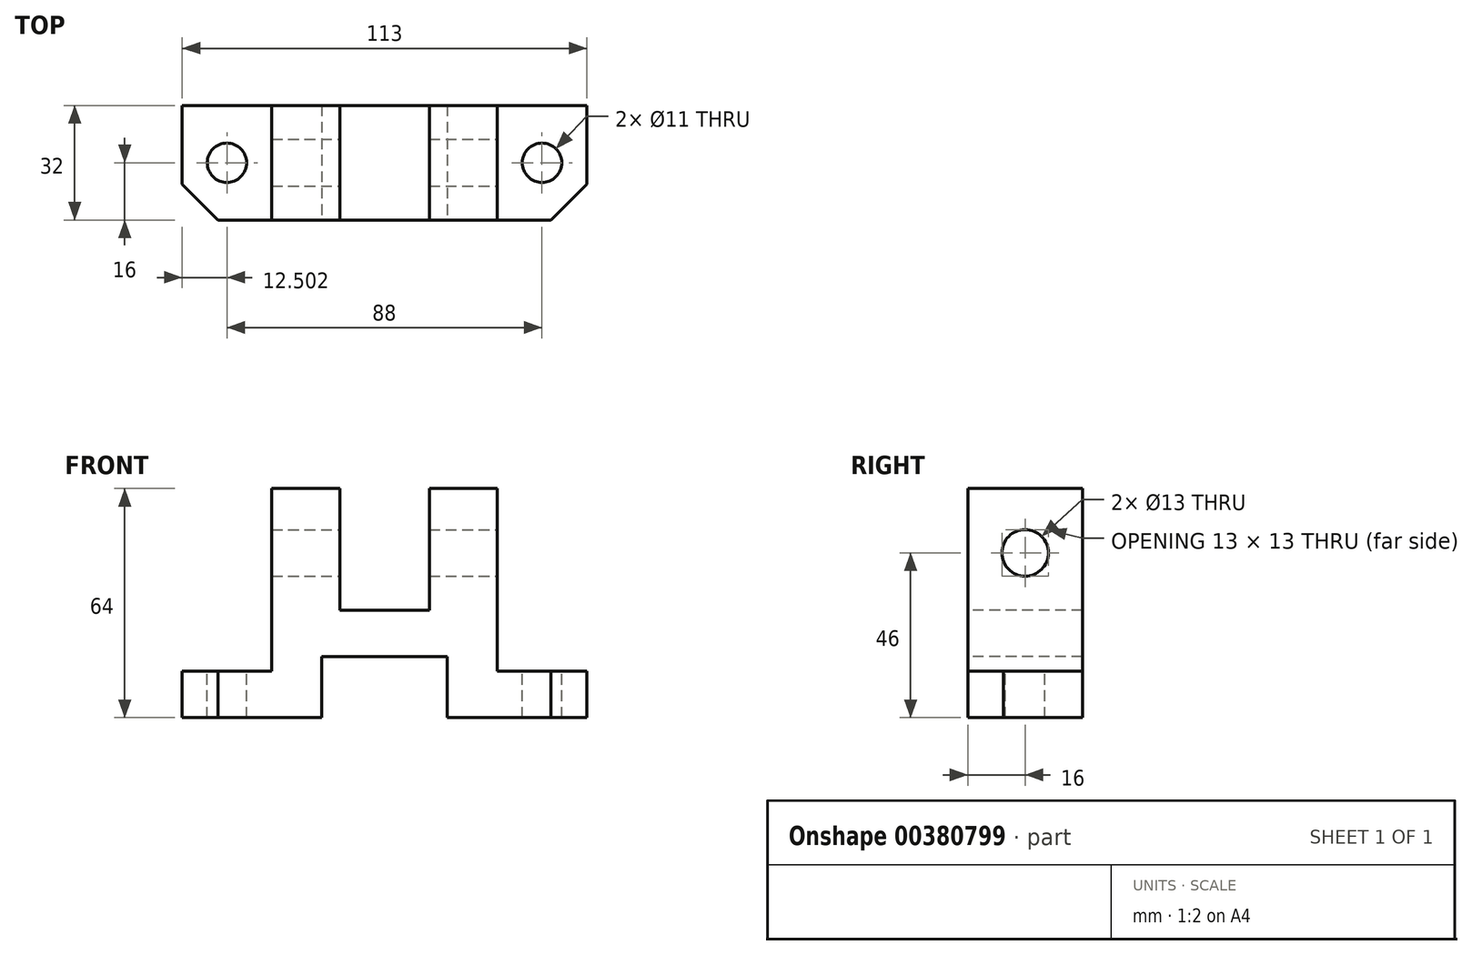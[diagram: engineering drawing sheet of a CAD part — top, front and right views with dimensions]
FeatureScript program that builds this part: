
annotation { "Feature Type Name" : "Feature", "Feature Type Description" : "" }
export const myFeature = defineFeature(function(context is Context, id is Id, definition is map)
    precondition{}
    {
        {
            var Q0;
            Q0=qCreatedBy(makeId("Top.planeOp"),FACE);
            var sketch = newSketch(context, id + "F0", { "sketchPlane" : qUnion([Q0])});
            skLineSegment(sketch, "E0", {"start": v(-42.78, 0) * mm, "end": v(70.22, 0) * mm});
            skLineSegment(sketch, "E1", {"start": v(70.22, 0) * mm, "end": v(70.22, 32) * mm});
            skLineSegment(sketch, "E2", {"start": v(70.22, 32) * mm, "end": v(-42.78, 32) * mm});
            skLineSegment(sketch, "E3", {"start": v(-42.78, 32) * mm, "end": v(-42.78, 0) * mm});
            skSolve(sketch);
        }
        {
            var Q0;
            Q0 = qSketchRegion(id + "F0", true);
            extrude(context, id + "F1", {"entities" : qUnion([Q0]), "depth" : 64 * mm});
        }
        {
            var Q0;
            Q0=makeQuery(id+"F1.opExtrude","SWEPT_FACE",FACE,{"disambiguationData":[OSD([sQuery(id+"F0.wireOp",EDGE,"E0")])]});
            var sketch = newSketch(context, id + "F2", { "sketchPlane" : qUnion([Q0])});
            skLineSegment(sketch, "E4", {"start": v(70.22, 0) * mm, "end": v(31.22, 0) * mm});
            skLineSegment(sketch, "E5", {"start": v(31.22, 0) * mm, "end": v(31.22, 17) * mm});
            skLineSegment(sketch, "E6", {"start": v(31.22, 17) * mm, "end": v(-3.78, 17) * mm});
            skLineSegment(sketch, "E7", {"start": v(-3.78, 17) * mm, "end": v(-3.78, 0) * mm});
            skLineSegment(sketch, "E8", {"start": v(70.22, 64) * mm, "end": v(45.22, 64) * mm});
            skLineSegment(sketch, "E9", {"start": v(45.22, 64) * mm, "end": v(45.22, 13) * mm});
            skLineSegment(sketch, "E10", {"start": v(45.22, 13) * mm, "end": v(70.22, 13) * mm});
            skLineSegment(sketch, "E11", {"start": v(45.22, 64) * mm, "end": v(26.22, 64) * mm});
            skLineSegment(sketch, "E12", {"start": v(26.22, 64) * mm, "end": v(26.22, 30) * mm});
            skLineSegment(sketch, "E13", {"start": v(26.22, 30) * mm, "end": v(1.22, 30) * mm});
            skLineSegment(sketch, "E14", {"start": v(1.22, 30) * mm, "end": v(1.22, 64) * mm});
            skLineSegment(sketch, "E15", {"start": v(1.22, 64) * mm, "end": v(-17.78, 64) * mm});
            skLineSegment(sketch, "E16", {"start": v(-17.78, 64) * mm, "end": v(-17.78, 13) * mm});
            skLineSegment(sketch, "E17", {"start": v(-17.78, 13) * mm, "end": v(-42.78, 13) * mm});
            skSolve(sketch);
        }
        {
            var Q0;
            Q0 = qSketchRegion(id + "F2", true);
            var Q1;
            {var subQ0=sQuery(id+"F2.wireOp",EDGE,"E16");Q1=makeQuery(id+"F2.imprint","IMPRINT",FACE,{"disambiguationData":[TD([[makeQuery(id+"F2.imprint","IMPRINT",EDGE,{"derivedFrom":subQ0}),-1.0]])]});}
            var Q2;
            {var subQ0=sQuery(id+"F2.wireOp",EDGE,"E12");Q2=makeQuery(id+"F2.imprint","IMPRINT",FACE,{"disambiguationData":[TD([[makeQuery(id+"F2.imprint","IMPRINT",EDGE,{"derivedFrom":subQ0}),-1.0]])]});}
            var Q3;
            {var subQ0=sQuery(id+"F2.wireOp",EDGE,"E5");Q3=makeQuery(id+"F2.imprint","IMPRINT",FACE,{"disambiguationData":[TD([[makeQuery(id+"F2.imprint","IMPRINT",EDGE,{"derivedFrom":subQ0}),1.0]])]});}
            var Q4;
            {var subQ0=sQuery(id+"F2.wireOp",EDGE,"E8");Q4=makeQuery(id+"F2.imprint","IMPRINT",FACE,{"disambiguationData":[TD([[makeQuery(id+"F2.imprint","IMPRINT",EDGE,{"derivedFrom":subQ0}),-1.0]])]});}
            extrude(context, id + "F3", {"entities" : qUnion([Q0, Q1, Q2, Q3, Q4]), "operationType" : NewBodyOperationType.REMOVE, "endBound" : BoundingType.THROUGH_ALL, "oppositeDirection" : true, "depth" : 25 * mm});
        }
        {
            var Q0;
            Q0=makeQuery(id+"F3.boolean.opBoolean","COPY",FACE,{"derivedFrom":makeQuery(id+"F3.opExtrude","SWEPT_FACE",FACE,{"disambiguationData":[OSD([sQuery(id+"F2.wireOp",EDGE,"E17")])]})});
            var sketch = newSketch(context, id + "F4", { "sketchPlane" : qUnion([Q0])});
            skLineSegment(sketch, "E18", {"start": v(-42.78, 0) * mm, "end": v(-32.78, 0) * mm});
            skLineSegment(sketch, "E19", {"start": v(-32.78, 0) * mm, "end": v(-42.78, 10) * mm});
            skLineSegment(sketch, "E20", {"start": v(-17.78, 32) * mm, "end": v(-42.78, 0) * mm, "construction": true});
            skLineSegment(sketch, "E21", {"start": v(-42.78, 32) * mm, "end": v(-17.78, 0) * mm, "construction": true});
            skCircle(sketch, "E22", {"center": v(-30.28, 16) * mm, "radius": 5.5 * mm});
            skSolve(sketch);
        }
        {
            var Q0;
            Q0=makeQuery(id+"F3.boolean.opBoolean","COPY",FACE,{"derivedFrom":makeQuery(id+"F3.opExtrude","SWEPT_FACE",FACE,{"disambiguationData":[OSD([sQuery(id+"F2.wireOp",EDGE,"E10")])]})});
            var sketch = newSketch(context, id + "F5", { "sketchPlane" : qUnion([Q0])});
            skLineSegment(sketch, "E23", {"start": v(70.22, 0) * mm, "end": v(60.22, 0) * mm});
            skLineSegment(sketch, "E24", {"start": v(60.22, 0) * mm, "end": v(70.22, 10) * mm});
            skLineSegment(sketch, "E25", {"start": v(45.22, 32) * mm, "end": v(70.22, 0) * mm, "construction": true});
            skLineSegment(sketch, "E26", {"start": v(45.22, 0) * mm, "end": v(70.22, 32) * mm, "construction": true});
            skCircle(sketch, "E27", {"center": v(57.72, 16) * mm, "radius": 5.5 * mm});
            skSolve(sketch);
        }
        {
            var Q0;
            Q0=makeQuery(id+"F3.boolean.opBoolean","COPY",FACE,{"derivedFrom":makeQuery(id+"F3.opExtrude","SWEPT_FACE",FACE,{"disambiguationData":[OSD([sQuery(id+"F2.wireOp",EDGE,"E9")])]})});
            var sketch = newSketch(context, id + "F6", { "sketchPlane" : qUnion([Q0])});
            skLineSegment(sketch, "E28", {"start": v(0, 64) * mm, "end": v(32, 13) * mm});
            skLineSegment(sketch, "E29", {"start": v(0, 13) * mm, "end": v(32, 64) * mm});
            skLineSegment(sketch, "E30", {"start": v(16, 38.5) * mm, "end": v(16, 0) * mm});
            skPoint(sketch, "E30.endSnap0", {"position": v(16, 13) * mm});
            skLineSegment(sketch, "E31", {"start": v(16, 0) * mm, "end": v(16, 46) * mm});
            skCircle(sketch, "E32", {"center": v(16, 46) * mm, "radius": 6.5 * mm});
            skSolve(sketch);
        }
        {
            var Q0;
            Q0=makeQuery(id+"F5.imprint","IMPRINT",FACE,{"disambiguationData":[TD([[makeQuery(id+"F5.imprint","IMPRINT",EDGE,{"derivedFrom":sQuery(id+"F5.wireOp",EDGE,"E27")}),1.0]])]});
            var Q1;
            {var subQ0=sQuery(id+"F5.wireOp",EDGE,"E23");Q1=makeQuery(id+"F5.imprint","IMPRINT",FACE,{"disambiguationData":[TD([[makeQuery(id+"F5.imprint","IMPRINT",EDGE,{"derivedFrom":subQ0}),1.0]])]});}
            var Q2;
            Q2=makeQuery(id+"F4.imprint","IMPRINT",FACE,{"disambiguationData":[TD([[makeQuery(id+"F4.imprint","IMPRINT",EDGE,{"derivedFrom":sQuery(id+"F4.wireOp",EDGE,"E22")}),1.0]])]});
            var Q3;
            {var subQ0=sQuery(id+"F4.wireOp",EDGE,"E18");Q3=makeQuery(id+"F4.imprint","IMPRINT",FACE,{"disambiguationData":[TD([[makeQuery(id+"F4.imprint","IMPRINT",EDGE,{"derivedFrom":subQ0}),-1.0]])]});}
            extrude(context, id + "F7", {"entities" : qUnion([Q0, Q1, Q2, Q3]), "operationType" : NewBodyOperationType.REMOVE, "oppositeDirection" : true, "depth" : 25 * mm});
        }
        {
            var Q0;
            {var subQ0=sQuery(id+"F6.wireOp",EDGE,"E32");var subQ2=sQuery(id+"F6.wireOp",EDGE,"E28");var subQ4=makeQuery(id+"F6.imprint","INTERSECT",VERTEX,{"disambiguationData":[OD(0.0)],"derivedFrom":[subQ2,subQ0]});Q0=makeQuery(id+"F6.imprint","IMPRINT",FACE,{"disambiguationData":[TD([[makeQuery(id+"F6.imprint","IMPRINT",EDGE,{"disambiguationData":[TD([[subQ4,-1.0]])],"derivedFrom":subQ2}),1.0]])]});}
            var Q1;
            {var subQ0=sQuery(id+"F6.wireOp",EDGE,"E32");var subQ1=sQuery(id+"F6.wireOp",EDGE,"E28");var subQ2=makeQuery(id+"F6.imprint","INTERSECT",VERTEX,{"disambiguationData":[OD(0.0)],"derivedFrom":[subQ1,subQ0]});Q1=makeQuery(id+"F6.imprint","IMPRINT",FACE,{"disambiguationData":[TD([[makeQuery(id+"F6.imprint","IMPRINT",EDGE,{"disambiguationData":[TD([[subQ2,-1.0]])],"derivedFrom":subQ1}),-1.0]])]});}
            var Q2;
            {var subQ0=sQuery(id+"F6.wireOp",EDGE,"E32");var subQ1=sQuery(id+"F6.wireOp",EDGE,"E29");var subQ2=makeQuery(id+"F6.imprint","INTERSECT",VERTEX,{"disambiguationData":[OD(0.0)],"derivedFrom":[subQ1,subQ0]});Q2=makeQuery(id+"F6.imprint","IMPRINT",FACE,{"disambiguationData":[TD([[makeQuery(id+"F6.imprint","IMPRINT",EDGE,{"disambiguationData":[TD([[subQ2,-1.0]])],"derivedFrom":subQ1}),-1.0]])]});}
            extrude(context, id + "F8", {"entities" : qUnion([Q0, Q1, Q2]), "operationType" : NewBodyOperationType.REMOVE, "endBound" : BoundingType.THROUGH_ALL, "oppositeDirection" : true, "depth" : 25 * mm});
        }
    });
